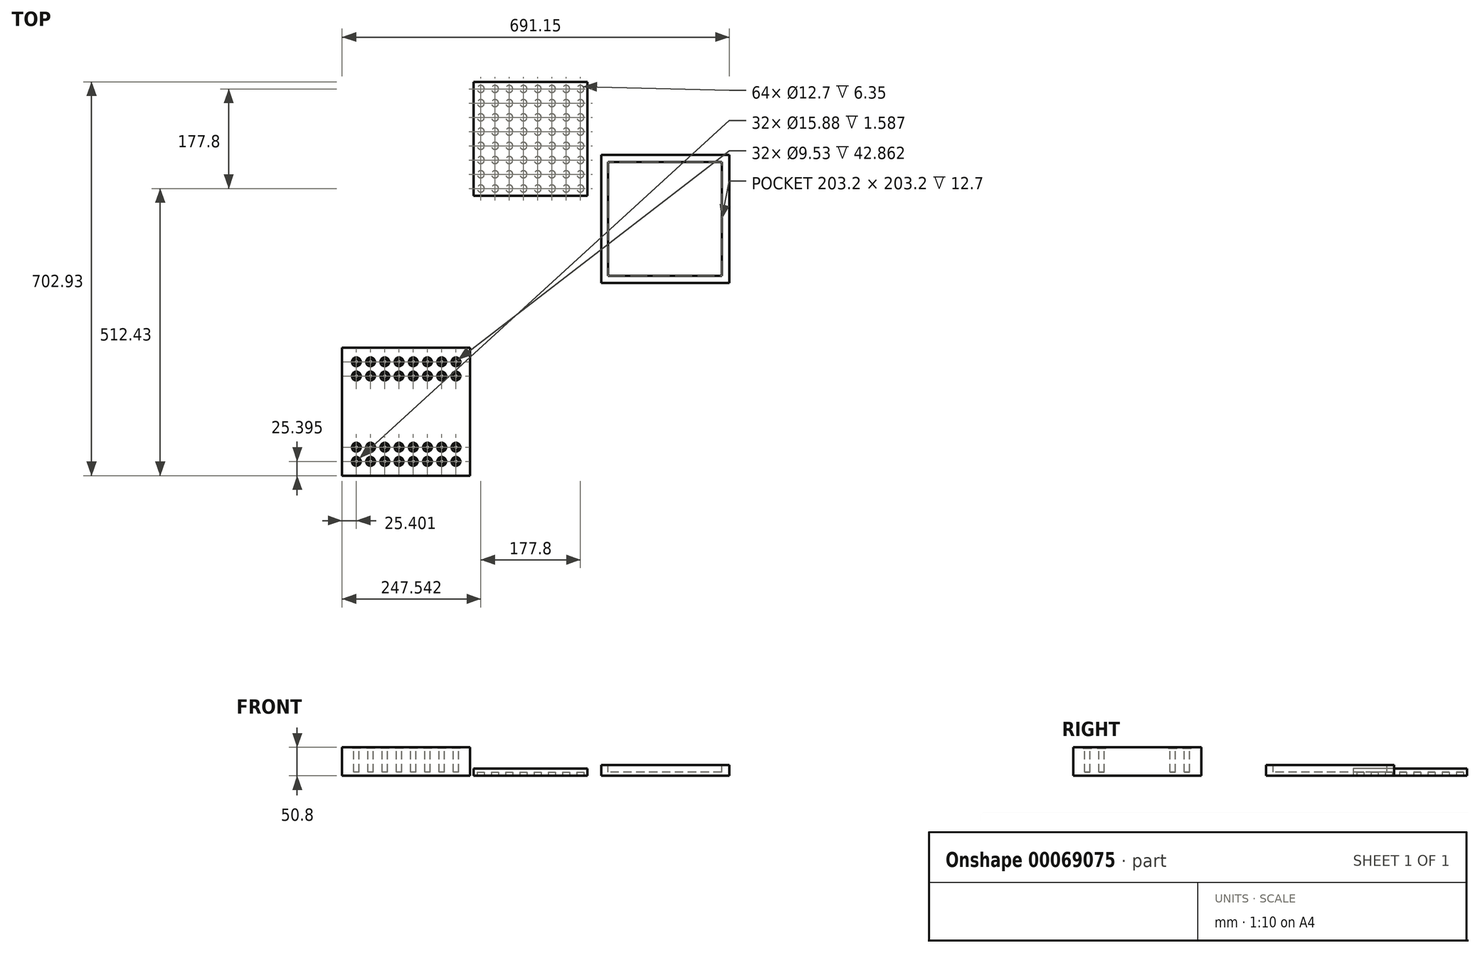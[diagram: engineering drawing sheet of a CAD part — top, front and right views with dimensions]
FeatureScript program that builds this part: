
annotation { "Feature Type Name" : "Feature", "Feature Type Description" : "" }
export const myFeature = defineFeature(function(context is Context, id is Id, definition is map)
    precondition{}
    {
        {
            var Q0;
            Q0=qCreatedBy(makeId("Top.planeOp"),FACE);
            var sketch = newSketch(context, id + "F0", { "sketchPlane" : qUnion([Q0])});
            skLineSegment(sketch, "E0.bottom", {"start": v(-192.4, 107.4) * mm, "end": v(10.8, 107.4) * mm});
            skLineSegment(sketch, "E0.top", {"start": v(-192.4, -95.8) * mm, "end": v(10.8, -95.8) * mm});
            skLineSegment(sketch, "E0.left", {"start": v(-192.4, 107.4) * mm, "end": v(-192.4, -95.8) * mm});
            skLineSegment(sketch, "E0.right", {"start": v(10.8, 107.4) * mm, "end": v(10.8, -95.8) * mm});
            skSolve(sketch);
        }
        {
            var Q0;
            Q0=makeQuery(id+"F0.imprint","IMPRINT",FACE,{"disambiguationData":[TD([[makeQuery(id+"F0.imprint","IMPRINT",EDGE,{"derivedFrom":sQuery(id+"F0.wireOp",EDGE,"E0.bottom")}),-1.0]])]});
            extrude(context, id + "F1", {"entities" : qUnion([Q0]), "depth" : 12.7 * mm});
        }
        {
            var Q0;
            Q0=makeQuery(id+"F1.opExtrude","CAP_FACE",FACE,{"disambiguationData":[OSD([sQuery(id+"F0.wireOp",EDGE,"E0.bottom"),sQuery(id+"F0.wireOp",EDGE,"E0.top"),sQuery(id+"F0.wireOp",EDGE,"E0.left"),sQuery(id+"F0.wireOp",EDGE,"E0.right")])],"isStart":true});
            var sketch = newSketch(context, id + "F2", { "sketchPlane" : qUnion([Q0])});
            skCircle(sketch, "E1", {"center": v(-179.7, 83.1) * mm, "radius": 6.35 * mm});
            skCircle(sketch, "E2.0.1.0", {"center": v(-179.7, 57.7) * mm, "radius": 6.35 * mm});
            skCircle(sketch, "E2.0.2.0", {"center": v(-179.7, 32.3) * mm, "radius": 6.35 * mm});
            skCircle(sketch, "E2.0.3.0", {"center": v(-179.7, 6.9) * mm, "radius": 6.35 * mm});
            skCircle(sketch, "E2.0.4.0", {"center": v(-179.7, -18.5) * mm, "radius": 6.35 * mm});
            skCircle(sketch, "E2.0.5.0", {"center": v(-179.7, -43.9) * mm, "radius": 6.35 * mm});
            skCircle(sketch, "E2.0.6.0", {"center": v(-179.7, -69.3) * mm, "radius": 6.35 * mm});
            skCircle(sketch, "E2.0.7.0", {"center": v(-179.7, -94.7) * mm, "radius": 6.35 * mm});
            skCircle(sketch, "E2.1.0.0", {"center": v(-154.3, 83.1) * mm, "radius": 6.35 * mm});
            skCircle(sketch, "E2.1.1.0", {"center": v(-154.3, 57.7) * mm, "radius": 6.35 * mm});
            skCircle(sketch, "E2.1.2.0", {"center": v(-154.3, 32.3) * mm, "radius": 6.35 * mm});
            skCircle(sketch, "E2.1.3.0", {"center": v(-154.3, 6.9) * mm, "radius": 6.35 * mm});
            skCircle(sketch, "E2.1.4.0", {"center": v(-154.3, -18.5) * mm, "radius": 6.35 * mm});
            skCircle(sketch, "E2.1.5.0", {"center": v(-154.3, -43.9) * mm, "radius": 6.35 * mm});
            skCircle(sketch, "E2.1.6.0", {"center": v(-154.3, -69.3) * mm, "radius": 6.35 * mm});
            skCircle(sketch, "E2.1.7.0", {"center": v(-154.3, -94.7) * mm, "radius": 6.35 * mm});
            skCircle(sketch, "E2.2.0.0", {"center": v(-128.9, 83.1) * mm, "radius": 6.35 * mm});
            skCircle(sketch, "E2.2.1.0", {"center": v(-128.9, 57.7) * mm, "radius": 6.35 * mm});
            skCircle(sketch, "E2.2.2.0", {"center": v(-128.9, 32.3) * mm, "radius": 6.35 * mm});
            skCircle(sketch, "E2.2.3.0", {"center": v(-128.9, 6.9) * mm, "radius": 6.35 * mm});
            skCircle(sketch, "E2.2.4.0", {"center": v(-128.9, -18.5) * mm, "radius": 6.35 * mm});
            skCircle(sketch, "E2.2.5.0", {"center": v(-128.9, -43.9) * mm, "radius": 6.35 * mm});
            skCircle(sketch, "E2.2.6.0", {"center": v(-128.9, -69.3) * mm, "radius": 6.35 * mm});
            skCircle(sketch, "E2.2.7.0", {"center": v(-128.9, -94.7) * mm, "radius": 6.35 * mm});
            skCircle(sketch, "E2.3.0.0", {"center": v(-103.5, 83.1) * mm, "radius": 6.35 * mm});
            skCircle(sketch, "E2.3.1.0", {"center": v(-103.5, 57.7) * mm, "radius": 6.35 * mm});
            skCircle(sketch, "E2.3.2.0", {"center": v(-103.5, 32.3) * mm, "radius": 6.35 * mm});
            skCircle(sketch, "E2.3.3.0", {"center": v(-103.5, 6.9) * mm, "radius": 6.35 * mm});
            skCircle(sketch, "E2.3.4.0", {"center": v(-103.5, -18.5) * mm, "radius": 6.35 * mm});
            skCircle(sketch, "E2.3.5.0", {"center": v(-103.5, -43.9) * mm, "radius": 6.35 * mm});
            skCircle(sketch, "E2.3.6.0", {"center": v(-103.5, -69.3) * mm, "radius": 6.35 * mm});
            skCircle(sketch, "E2.3.7.0", {"center": v(-103.5, -94.7) * mm, "radius": 6.35 * mm});
            skCircle(sketch, "E2.4.0.0", {"center": v(-78.1, 83.1) * mm, "radius": 6.35 * mm});
            skCircle(sketch, "E2.4.1.0", {"center": v(-78.1, 57.7) * mm, "radius": 6.35 * mm});
            skCircle(sketch, "E2.4.2.0", {"center": v(-78.1, 32.3) * mm, "radius": 6.35 * mm});
            skCircle(sketch, "E2.4.3.0", {"center": v(-78.1, 6.9) * mm, "radius": 6.35 * mm});
            skCircle(sketch, "E2.4.4.0", {"center": v(-78.1, -18.5) * mm, "radius": 6.35 * mm});
            skCircle(sketch, "E2.4.5.0", {"center": v(-78.1, -43.9) * mm, "radius": 6.35 * mm});
            skCircle(sketch, "E2.4.6.0", {"center": v(-78.1, -69.3) * mm, "radius": 6.35 * mm});
            skCircle(sketch, "E2.4.7.0", {"center": v(-78.1, -94.7) * mm, "radius": 6.35 * mm});
            skCircle(sketch, "E2.5.0.0", {"center": v(-52.7, 83.1) * mm, "radius": 6.35 * mm});
            skCircle(sketch, "E2.5.1.0", {"center": v(-52.7, 57.7) * mm, "radius": 6.35 * mm});
            skCircle(sketch, "E2.5.2.0", {"center": v(-52.7, 32.3) * mm, "radius": 6.35 * mm});
            skCircle(sketch, "E2.5.3.0", {"center": v(-52.7, 6.9) * mm, "radius": 6.35 * mm});
            skCircle(sketch, "E2.5.4.0", {"center": v(-52.7, -18.5) * mm, "radius": 6.35 * mm});
            skCircle(sketch, "E2.5.5.0", {"center": v(-52.7, -43.9) * mm, "radius": 6.35 * mm});
            skCircle(sketch, "E2.5.6.0", {"center": v(-52.7, -69.3) * mm, "radius": 6.35 * mm});
            skCircle(sketch, "E2.5.7.0", {"center": v(-52.7, -94.7) * mm, "radius": 6.35 * mm});
            skCircle(sketch, "E2.6.0.0", {"center": v(-27.3, 83.1) * mm, "radius": 6.35 * mm});
            skCircle(sketch, "E2.6.1.0", {"center": v(-27.3, 57.7) * mm, "radius": 6.35 * mm});
            skCircle(sketch, "E2.6.2.0", {"center": v(-27.3, 32.3) * mm, "radius": 6.35 * mm});
            skCircle(sketch, "E2.6.3.0", {"center": v(-27.3, 6.9) * mm, "radius": 6.35 * mm});
            skCircle(sketch, "E2.6.4.0", {"center": v(-27.3, -18.5) * mm, "radius": 6.35 * mm});
            skCircle(sketch, "E2.6.5.0", {"center": v(-27.3, -43.9) * mm, "radius": 6.35 * mm});
            skCircle(sketch, "E2.6.6.0", {"center": v(-27.3, -69.3) * mm, "radius": 6.35 * mm});
            skCircle(sketch, "E2.6.7.0", {"center": v(-27.3, -94.7) * mm, "radius": 6.35 * mm});
            skCircle(sketch, "E2.7.0.0", {"center": v(-1.9, 83.1) * mm, "radius": 6.35 * mm});
            skCircle(sketch, "E2.7.1.0", {"center": v(-1.9, 57.7) * mm, "radius": 6.35 * mm});
            skCircle(sketch, "E2.7.2.0", {"center": v(-1.9, 32.3) * mm, "radius": 6.35 * mm});
            skCircle(sketch, "E2.7.3.0", {"center": v(-1.9, 6.9) * mm, "radius": 6.35 * mm});
            skCircle(sketch, "E2.7.4.0", {"center": v(-1.9, -18.5) * mm, "radius": 6.35 * mm});
            skCircle(sketch, "E2.7.5.0", {"center": v(-1.9, -43.9) * mm, "radius": 6.35 * mm});
            skCircle(sketch, "E2.7.6.0", {"center": v(-1.9, -69.3) * mm, "radius": 6.35 * mm});
            skCircle(sketch, "E2.7.7.0", {"center": v(-1.9, -94.7) * mm, "radius": 6.35 * mm});
            skLineSegment(sketch, "E2.direction1", {"start": v(-179.7, 83.1) * mm, "end": v(-154.3, 83.1) * mm, "construction": true});
            skLineSegment(sketch, "E2.direction2", {"start": v(-179.7, 83.1) * mm, "end": v(-179.7, 57.7) * mm, "construction": true});
            skSolve(sketch);
        }
        {
            var Q0;
            Q0 = qSketchRegion(id + "F2", true);
            extrude(context, id + "F3", {"entities" : qUnion([Q0]), "operationType" : NewBodyOperationType.REMOVE, "oppositeDirection" : true, "depth" : 6.35 * mm});
        }
        {
            var Q0;
            Q0=qCreatedBy(makeId("Top.planeOp"),FACE);
            var sketch = newSketch(context, id + "F4", { "sketchPlane" : qUnion([Q0])});
            skLineSegment(sketch, "E3.bottom", {"start": v(35.3, -251.37) * mm, "end": v(263.9, -251.37) * mm});
            skLineSegment(sketch, "E3.top", {"start": v(35.3, -22.77) * mm, "end": v(263.9, -22.77) * mm});
            skLineSegment(sketch, "E3.left", {"start": v(35.3, -251.37) * mm, "end": v(35.3, -22.77) * mm});
            skLineSegment(sketch, "E3.right", {"start": v(263.9, -251.37) * mm, "end": v(263.9, -22.77) * mm});
            skSolve(sketch);
        }
        {
            var Q0;
            Q0=makeQuery(id+"F4.imprint","IMPRINT",FACE,{"disambiguationData":[TD([[makeQuery(id+"F4.imprint","IMPRINT",EDGE,{"derivedFrom":sQuery(id+"F4.wireOp",EDGE,"E3.bottom")}),1.0]])]});
            extrude(context, id + "F5", {"entities" : qUnion([Q0]), "depth" : 19.05 * mm});
        }
        {
            var Q0;
            Q0=makeQuery(id+"F5.opExtrude","CAP_FACE",FACE,{"disambiguationData":[OSD([sQuery(id+"F4.wireOp",EDGE,"E3.bottom"),sQuery(id+"F4.wireOp",EDGE,"E3.top"),sQuery(id+"F4.wireOp",EDGE,"E3.left"),sQuery(id+"F4.wireOp",EDGE,"E3.right")])],"isStart":false});
            var sketch = newSketch(context, id + "F6", { "sketchPlane" : qUnion([Q0])});
            skLineSegment(sketch, "E4.bottom", {"start": v(250.65, -35.47) * mm, "end": v(47.45, -35.47) * mm});
            skLineSegment(sketch, "E4.top", {"start": v(250.65, -238.67) * mm, "end": v(47.45, -238.67) * mm});
            skLineSegment(sketch, "E4.left", {"start": v(250.65, -35.47) * mm, "end": v(250.65, -238.67) * mm});
            skLineSegment(sketch, "E4.right", {"start": v(47.45, -35.47) * mm, "end": v(47.45, -238.67) * mm});
            skSolve(sketch);
        }
        {
            var Q0;
            Q0 = qSketchRegion(id + "F6", true);
            extrude(context, id + "F7", {"entities" : qUnion([Q0]), "operationType" : NewBodyOperationType.REMOVE, "oppositeDirection" : true, "depth" : 12.7 * mm});
        }
        {
            var Q0;
            Q0=qCreatedBy(makeId("Top.planeOp"),FACE);
            var sketch = newSketch(context, id + "F8", { "sketchPlane" : qUnion([Q0])});
            skLineSegment(sketch, "E5.bottom", {"start": v(-198.65, -366.93) * mm, "end": v(-427.25, -366.93) * mm});
            skLineSegment(sketch, "E5.top", {"start": v(-198.65, -595.53) * mm, "end": v(-427.25, -595.53) * mm});
            skLineSegment(sketch, "E5.left", {"start": v(-198.65, -366.93) * mm, "end": v(-198.65, -595.53) * mm});
            skLineSegment(sketch, "E5.right", {"start": v(-427.25, -366.93) * mm, "end": v(-427.25, -595.53) * mm});
            skSolve(sketch);
        }
        {
            var Q0;
            Q0=makeQuery(id+"F8.imprint","IMPRINT",FACE,{"disambiguationData":[TD([[makeQuery(id+"F8.imprint","IMPRINT",EDGE,{"derivedFrom":sQuery(id+"F8.wireOp",EDGE,"E5.bottom")}),1.0]])]});
            extrude(context, id + "F9", {"entities" : qUnion([Q0]), "depth" : 50.8 * mm});
        }
        {
            var Q0;
            Q0=makeQuery(id+"F9.opExtrude","CAP_FACE",FACE,{"disambiguationData":[OSD([sQuery(id+"F8.wireOp",EDGE,"E5.bottom"),sQuery(id+"F8.wireOp",EDGE,"E5.top"),sQuery(id+"F8.wireOp",EDGE,"E5.left"),sQuery(id+"F8.wireOp",EDGE,"E5.right")])],"isStart":false});
            var sketch = newSketch(context, id + "F10", { "sketchPlane" : qUnion([Q0])});
            skCircle(sketch, "E6", {"center": v(-401.85, -392.33) * mm, "radius": 4.76 * mm});
            skCircle(sketch, "E7.0.1.0", {"center": v(-401.85, -417.73) * mm, "radius": 4.76 * mm});
            skCircle(sketch, "E7.1.0.0", {"center": v(-376.45, -392.33) * mm, "radius": 4.76 * mm});
            skCircle(sketch, "E7.1.1.0", {"center": v(-376.45, -417.73) * mm, "radius": 4.76 * mm});
            skCircle(sketch, "E7.2.0.0", {"center": v(-351.05, -392.33) * mm, "radius": 4.76 * mm});
            skCircle(sketch, "E7.2.1.0", {"center": v(-351.05, -417.73) * mm, "radius": 4.76 * mm});
            skCircle(sketch, "E7.3.0.0", {"center": v(-325.65, -392.33) * mm, "radius": 4.76 * mm});
            skCircle(sketch, "E7.3.1.0", {"center": v(-325.65, -417.73) * mm, "radius": 4.76 * mm});
            skCircle(sketch, "E7.4.0.0", {"center": v(-300.25, -392.33) * mm, "radius": 4.76 * mm});
            skCircle(sketch, "E7.4.1.0", {"center": v(-300.25, -417.73) * mm, "radius": 4.76 * mm});
            skCircle(sketch, "E7.5.0.0", {"center": v(-274.85, -392.33) * mm, "radius": 4.76 * mm});
            skCircle(sketch, "E7.5.1.0", {"center": v(-274.85, -417.73) * mm, "radius": 4.76 * mm});
            skCircle(sketch, "E7.6.0.0", {"center": v(-249.45, -392.33) * mm, "radius": 4.76 * mm});
            skCircle(sketch, "E7.6.1.0", {"center": v(-249.45, -417.73) * mm, "radius": 4.76 * mm});
            skCircle(sketch, "E7.7.0.0", {"center": v(-224.05, -392.33) * mm, "radius": 4.76 * mm});
            skCircle(sketch, "E7.7.1.0", {"center": v(-224.05, -417.73) * mm, "radius": 4.76 * mm});
            skLineSegment(sketch, "E7.direction1", {"start": v(-414.55, -379.63) * mm, "end": v(-389.15, -379.63) * mm, "construction": true});
            skLineSegment(sketch, "E7.direction2", {"start": v(-414.55, -379.63) * mm, "end": v(-414.55, -405.03) * mm, "construction": true});
            skCircle(sketch, "E8", {"center": v(-401.85, -570.13) * mm, "radius": 4.76 * mm});
            skCircle(sketch, "E9.0.1.0", {"center": v(-401.85, -544.73) * mm, "radius": 4.76 * mm});
            skCircle(sketch, "E9.1.0.0", {"center": v(-376.45, -570.13) * mm, "radius": 4.76 * mm});
            skCircle(sketch, "E9.1.1.0", {"center": v(-376.45, -544.73) * mm, "radius": 4.76 * mm});
            skCircle(sketch, "E9.2.0.0", {"center": v(-351.05, -570.13) * mm, "radius": 4.76 * mm});
            skCircle(sketch, "E9.2.1.0", {"center": v(-351.05, -544.73) * mm, "radius": 4.76 * mm});
            skCircle(sketch, "E9.3.0.0", {"center": v(-325.65, -570.13) * mm, "radius": 4.76 * mm});
            skCircle(sketch, "E9.3.1.0", {"center": v(-325.65, -544.73) * mm, "radius": 4.76 * mm});
            skCircle(sketch, "E9.4.0.0", {"center": v(-300.25, -570.13) * mm, "radius": 4.76 * mm});
            skCircle(sketch, "E9.4.1.0", {"center": v(-300.25, -544.73) * mm, "radius": 4.76 * mm});
            skCircle(sketch, "E9.5.0.0", {"center": v(-274.85, -570.13) * mm, "radius": 4.76 * mm});
            skCircle(sketch, "E9.5.1.0", {"center": v(-274.85, -544.73) * mm, "radius": 4.76 * mm});
            skCircle(sketch, "E9.6.0.0", {"center": v(-249.45, -570.13) * mm, "radius": 4.76 * mm});
            skCircle(sketch, "E9.6.1.0", {"center": v(-249.45, -544.73) * mm, "radius": 4.76 * mm});
            skCircle(sketch, "E9.7.0.0", {"center": v(-224.05, -570.13) * mm, "radius": 4.76 * mm});
            skCircle(sketch, "E9.7.1.0", {"center": v(-224.05, -544.73) * mm, "radius": 4.76 * mm});
            skLineSegment(sketch, "E9.direction1", {"start": v(-401.85, -570.13) * mm, "end": v(-376.45, -570.13) * mm, "construction": true});
            skLineSegment(sketch, "E9.direction2", {"start": v(-401.85, -570.13) * mm, "end": v(-401.85, -544.73) * mm, "construction": true});
            skSolve(sketch);
        }
        {
            var Q0;
            Q0 = qSketchRegion(id + "F10", true);
            extrude(context, id + "F11", {"entities" : qUnion([Q0]), "operationType" : NewBodyOperationType.REMOVE, "oppositeDirection" : true, "depth" : 44.45 * mm});
        }
        {
            var Q0;
            Q0=makeQuery(id+"F9.opExtrude","CAP_FACE",FACE,{"disambiguationData":[OSD([sQuery(id+"F8.wireOp",EDGE,"E5.bottom"),sQuery(id+"F8.wireOp",EDGE,"E5.top"),sQuery(id+"F8.wireOp",EDGE,"E5.left"),sQuery(id+"F8.wireOp",EDGE,"E5.right")])],"isStart":false});
            var sketch = newSketch(context, id + "F12", { "sketchPlane" : qUnion([Q0])});
            skCircle(sketch, "E10", {"center": v(-401.85, -392.33) * mm, "radius": 7.94 * mm});
            skCircle(sketch, "E11.0.1.0", {"center": v(-401.85, -417.73) * mm, "radius": 7.94 * mm});
            skCircle(sketch, "E11.1.0.0", {"center": v(-376.45, -392.33) * mm, "radius": 7.94 * mm});
            skCircle(sketch, "E11.1.1.0", {"center": v(-376.45, -417.73) * mm, "radius": 7.94 * mm});
            skCircle(sketch, "E11.2.0.0", {"center": v(-351.05, -392.33) * mm, "radius": 7.94 * mm});
            skCircle(sketch, "E11.2.1.0", {"center": v(-351.05, -417.73) * mm, "radius": 7.94 * mm});
            skCircle(sketch, "E11.3.0.0", {"center": v(-325.65, -392.33) * mm, "radius": 7.94 * mm});
            skCircle(sketch, "E11.3.1.0", {"center": v(-325.65, -417.73) * mm, "radius": 7.94 * mm});
            skCircle(sketch, "E11.4.0.0", {"center": v(-300.25, -392.33) * mm, "radius": 7.94 * mm});
            skCircle(sketch, "E11.4.1.0", {"center": v(-300.25, -417.73) * mm, "radius": 7.94 * mm});
            skCircle(sketch, "E11.5.0.0", {"center": v(-274.85, -392.33) * mm, "radius": 7.94 * mm});
            skCircle(sketch, "E11.5.1.0", {"center": v(-274.85, -417.73) * mm, "radius": 7.94 * mm});
            skCircle(sketch, "E11.6.0.0", {"center": v(-249.45, -392.33) * mm, "radius": 7.94 * mm});
            skCircle(sketch, "E11.6.1.0", {"center": v(-249.45, -417.73) * mm, "radius": 7.94 * mm});
            skCircle(sketch, "E11.7.0.0", {"center": v(-224.05, -392.33) * mm, "radius": 7.94 * mm});
            skCircle(sketch, "E11.7.1.0", {"center": v(-224.05, -417.73) * mm, "radius": 7.94 * mm});
            skLineSegment(sketch, "E11.direction1", {"start": v(-401.85, -392.33) * mm, "end": v(-376.45, -392.33) * mm, "construction": true});
            skLineSegment(sketch, "E11.direction2", {"start": v(-401.85, -392.33) * mm, "end": v(-401.85, -417.73) * mm, "construction": true});
            skCircle(sketch, "E12", {"center": v(-401.85, -570.13) * mm, "radius": 7.94 * mm});
            skCircle(sketch, "E13.0.1.0", {"center": v(-401.85, -544.73) * mm, "radius": 7.94 * mm});
            skCircle(sketch, "E13.1.0.0", {"center": v(-376.45, -570.13) * mm, "radius": 7.94 * mm});
            skCircle(sketch, "E13.1.1.0", {"center": v(-376.45, -544.73) * mm, "radius": 7.94 * mm});
            skCircle(sketch, "E13.2.0.0", {"center": v(-351.05, -570.13) * mm, "radius": 7.94 * mm});
            skCircle(sketch, "E13.2.1.0", {"center": v(-351.05, -544.73) * mm, "radius": 7.94 * mm});
            skCircle(sketch, "E13.3.0.0", {"center": v(-325.65, -570.13) * mm, "radius": 7.94 * mm});
            skCircle(sketch, "E13.3.1.0", {"center": v(-325.65, -544.73) * mm, "radius": 7.94 * mm});
            skCircle(sketch, "E13.4.0.0", {"center": v(-300.25, -570.13) * mm, "radius": 7.94 * mm});
            skCircle(sketch, "E13.4.1.0", {"center": v(-300.25, -544.73) * mm, "radius": 7.94 * mm});
            skCircle(sketch, "E13.5.0.0", {"center": v(-274.85, -570.13) * mm, "radius": 7.94 * mm});
            skCircle(sketch, "E13.5.1.0", {"center": v(-274.85, -544.73) * mm, "radius": 7.94 * mm});
            skCircle(sketch, "E13.6.0.0", {"center": v(-249.45, -570.13) * mm, "radius": 7.94 * mm});
            skCircle(sketch, "E13.6.1.0", {"center": v(-249.45, -544.73) * mm, "radius": 7.94 * mm});
            skCircle(sketch, "E13.7.0.0", {"center": v(-224.05, -570.13) * mm, "radius": 7.94 * mm});
            skCircle(sketch, "E13.7.1.0", {"center": v(-224.05, -544.73) * mm, "radius": 7.94 * mm});
            skLineSegment(sketch, "E13.direction1", {"start": v(-401.85, -570.13) * mm, "end": v(-376.45, -570.13) * mm, "construction": true});
            skLineSegment(sketch, "E13.direction2", {"start": v(-401.85, -570.13) * mm, "end": v(-401.85, -544.73) * mm, "construction": true});
            skSolve(sketch);
        }
        {
            var Q0;
            Q0 = qSketchRegion(id + "F12", true);
            extrude(context, id + "F13", {"entities" : qUnion([Q0]), "operationType" : NewBodyOperationType.REMOVE, "oppositeDirection" : true, "depth" : 1.59 * mm});
        }
    });
